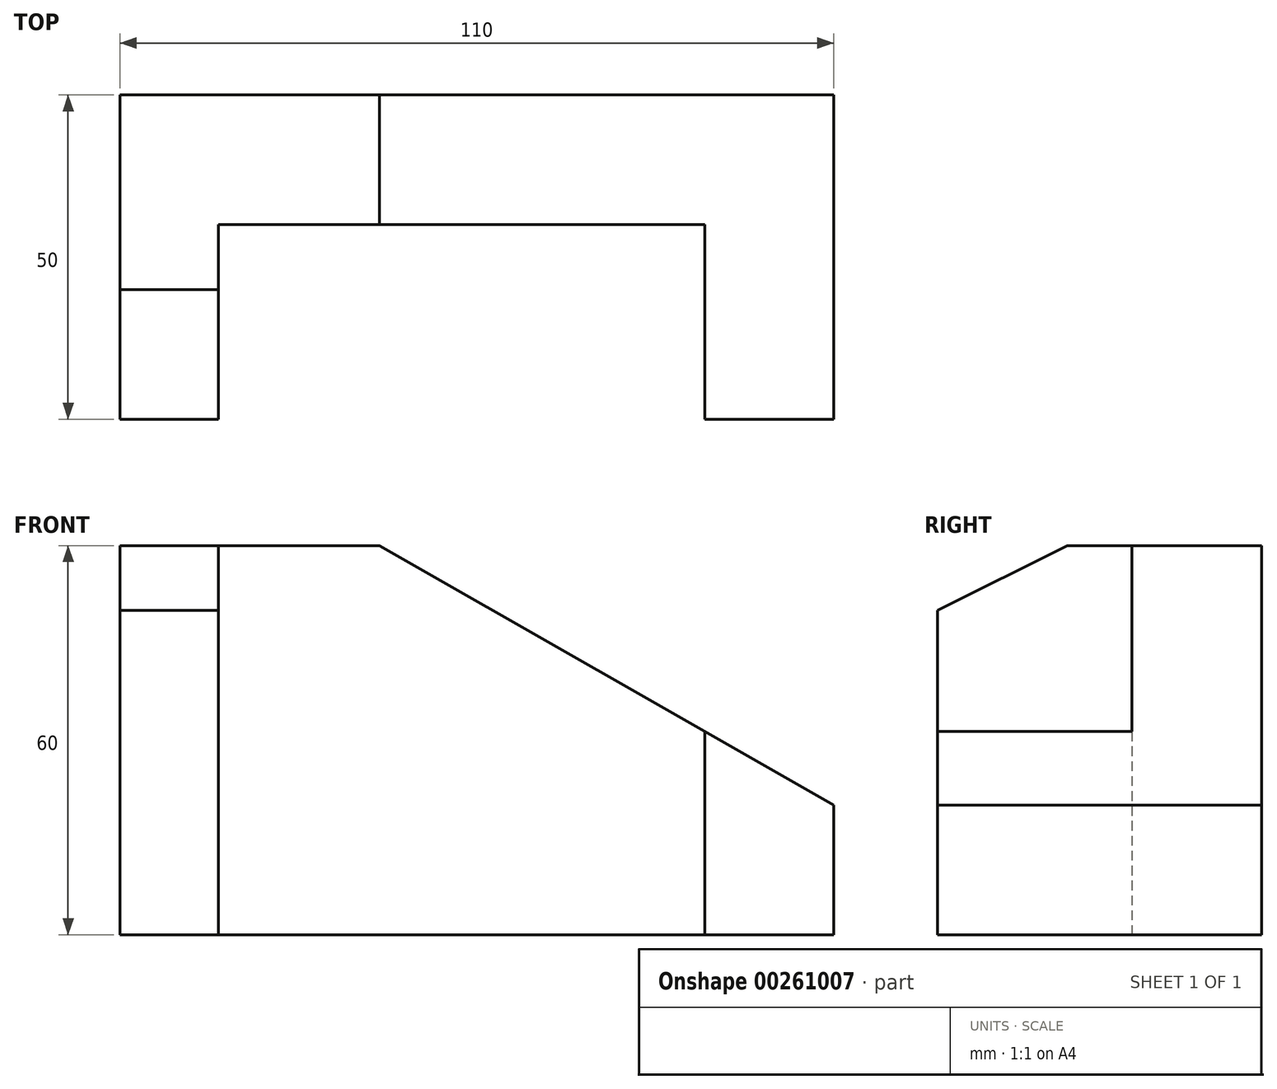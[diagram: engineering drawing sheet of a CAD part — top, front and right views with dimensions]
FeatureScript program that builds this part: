
annotation { "Feature Type Name" : "Feature", "Feature Type Description" : "" }
export const myFeature = defineFeature(function(context is Context, id is Id, definition is map)
    precondition{}
    {
        {
            var Q0;
            Q0=qCreatedBy(makeId("Front.planeOp"),FACE);
            var sketch = newSketch(context, id + "F0", { "sketchPlane" : qUnion([Q0])});
            skLineSegment(sketch, "E0", {"start": v(-55.16, 0) * mm, "end": v(54.84, 0) * mm});
            skLineSegment(sketch, "E1", {"start": v(-55.16, 0) * mm, "end": v(-55.16, 60) * mm});
            skLineSegment(sketch, "E2", {"start": v(-55.16, 60) * mm, "end": v(-15.16, 60) * mm});
            skLineSegment(sketch, "E3", {"start": v(54.84, 0) * mm, "end": v(54.84, 20) * mm});
            skLineSegment(sketch, "E4", {"start": v(-15.16, 60) * mm, "end": v(54.84, 20) * mm});
            skSolve(sketch);
        }
        {
            var Q0;
            Q0 = qSketchRegion(id + "F0", true);
            extrude(context, id + "F1", {"entities" : qUnion([Q0]), "depth" : 50 * mm});
        }
        {
            var Q0;
            Q0=qCreatedBy(makeId("Top.planeOp"),FACE);
            var sketch = newSketch(context, id + "F2", { "sketchPlane" : qUnion([Q0])});
            skPoint(sketch, "E5.middle", {"position": v(0, 0) * mm});
            skLineSegment(sketch, "E6.bottom", {"start": v(-40, -20) * mm, "end": v(35, -20) * mm});
            skLineSegment(sketch, "E6.top", {"start": v(-40, -50) * mm, "end": v(35, -50) * mm});
            skLineSegment(sketch, "E6.left", {"start": v(-40, -20) * mm, "end": v(-40, -50) * mm});
            skLineSegment(sketch, "E6.right", {"start": v(35, -20) * mm, "end": v(35, -50) * mm});
            skSolve(sketch);
        }
        {
            var Q0;
            Q0 = qSketchRegion(id + "F2", true);
            extrude(context, id + "F3", {"entities" : qUnion([Q0]), "operationType" : NewBodyOperationType.REMOVE, "depth" : 60 * mm});
        }
        {
            var Q0;
            Q0=qCreatedBy(makeId("Right.planeOp"),FACE);
            var sketch = newSketch(context, id + "F4", { "sketchPlane" : qUnion([Q0])});
            skLineSegment(sketch, "E7", {"start": v(-30, 60) * mm, "end": v(-50, 50) * mm});
            skLineSegment(sketch, "E8", {"start": v(-50, 50) * mm, "end": v(-50, 60) * mm});
            skLineSegment(sketch, "E9", {"start": v(-50, 60) * mm, "end": v(-30, 60) * mm});
            skSolve(sketch);
        }
        {
            var Q0;
            Q0 = qSketchRegion(id + "F4", true);
            extrude(context, id + "F5", {"entities" : qUnion([Q0]), "operationType" : NewBodyOperationType.REMOVE, "endBound" : BoundingType.SYMMETRIC, "depth" : 112 * mm});
        }
    });
